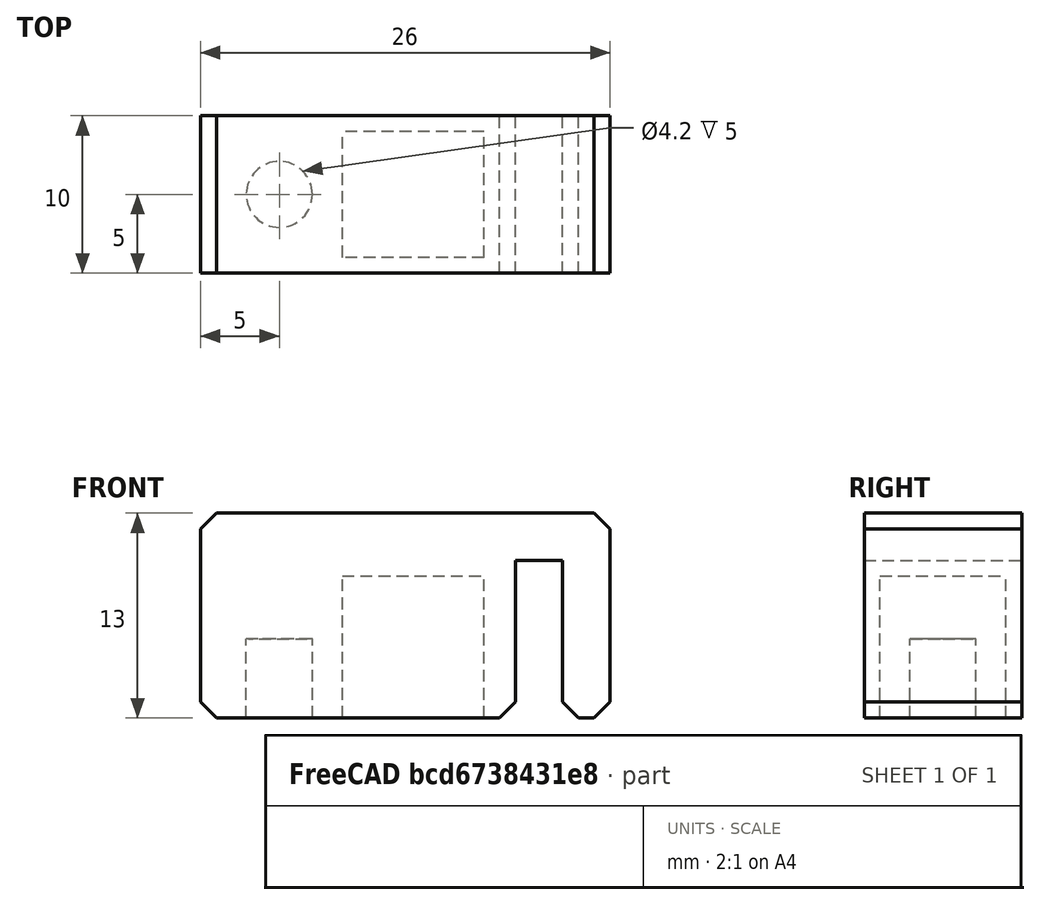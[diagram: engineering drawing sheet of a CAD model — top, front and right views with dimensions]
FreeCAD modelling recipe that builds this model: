
FCSTD DOCUMENT  (FreeCAD 0.16R6662 (Git))
Label: stangenhalter_einfach
License: CreativeCommons Attribution-ShareAlike
LicenseURL: http://creativecommons.org/licenses/by-sa/4.0/
objects: Part::Chamfer×5, Part::Cut×4, Part::Box×3, Part::Cylinder×2
note: 14 computed .brp shape members not serialized (recipe doc carries the construction recipe); baked Part::Feature solids carry a one-line shape summary decoded from their .brp

FEATURE [Part::Box] Box  label="Cube"
  Height = 10
  Length = 26
  Placement = pos=(0,0,0) rot=(1,0,0;1.5708rad)
  Width = 13
FEATURE [Part::Cylinder] Cylinder
  Angle = 360
  Height = 10
  Placement = pos=(5,-5,-5) rot=(0,0,1;0rad)
  Radius = 2
FEATURE [Part::Box] Box001  label="Cube001"
  Height = 11
  Length = 3
  Placement = pos=(20,-11,-1) rot=(0,0,1;0rad)
  Width = 12
FEATURE [Part::Cut] Cut
  Base = -> Box
  Tool = -> Cylinder
FEATURE [Part::Cut] Cut001
  Base = -> Cut
  Tool = -> Box001
FEATURE [Part::Chamfer] Chamfer
  Base = -> Cut001
  Edges = 2 edges r=1: [Edge1,Edge26]
FEATURE [Part::Chamfer] Chamfer001
  Base = -> Chamfer
  Edges = 1 edges r=1: [Edge30]
FEATURE [Part::Chamfer] Chamfer002
  Base = -> Chamfer001
  Edges = 1 edges r=1: [Edge31]
FEATURE [Part::Chamfer] Chamfer003
  Base = -> Chamfer002
  Edges = 1 edges r=1: [Edge25]
FEATURE [Part::Chamfer] Chamfer004
  Base = -> Chamfer003
  Edges = 1 edges r=1: [Edge16]
FEATURE [Part::Box] Box002  label="Cube002"
  Height = 10
  Length = 9
  Placement = pos=(9,-9,-1) rot=(0,0,1;0rad)
  Width = 8
FEATURE [Part::Cut] Cut002
  Base = -> Chamfer004
  Tool = -> Box002
FEATURE [Part::Cylinder] Cylinder001
  Angle = 360
  Height = 10
  Placement = pos=(5,-5,-5) rot=(0,0,1;0rad)
  Radius = 2.1
FEATURE [Part::Cut] Cut003
  Base = -> Cut002
  Tool = -> Cylinder001
